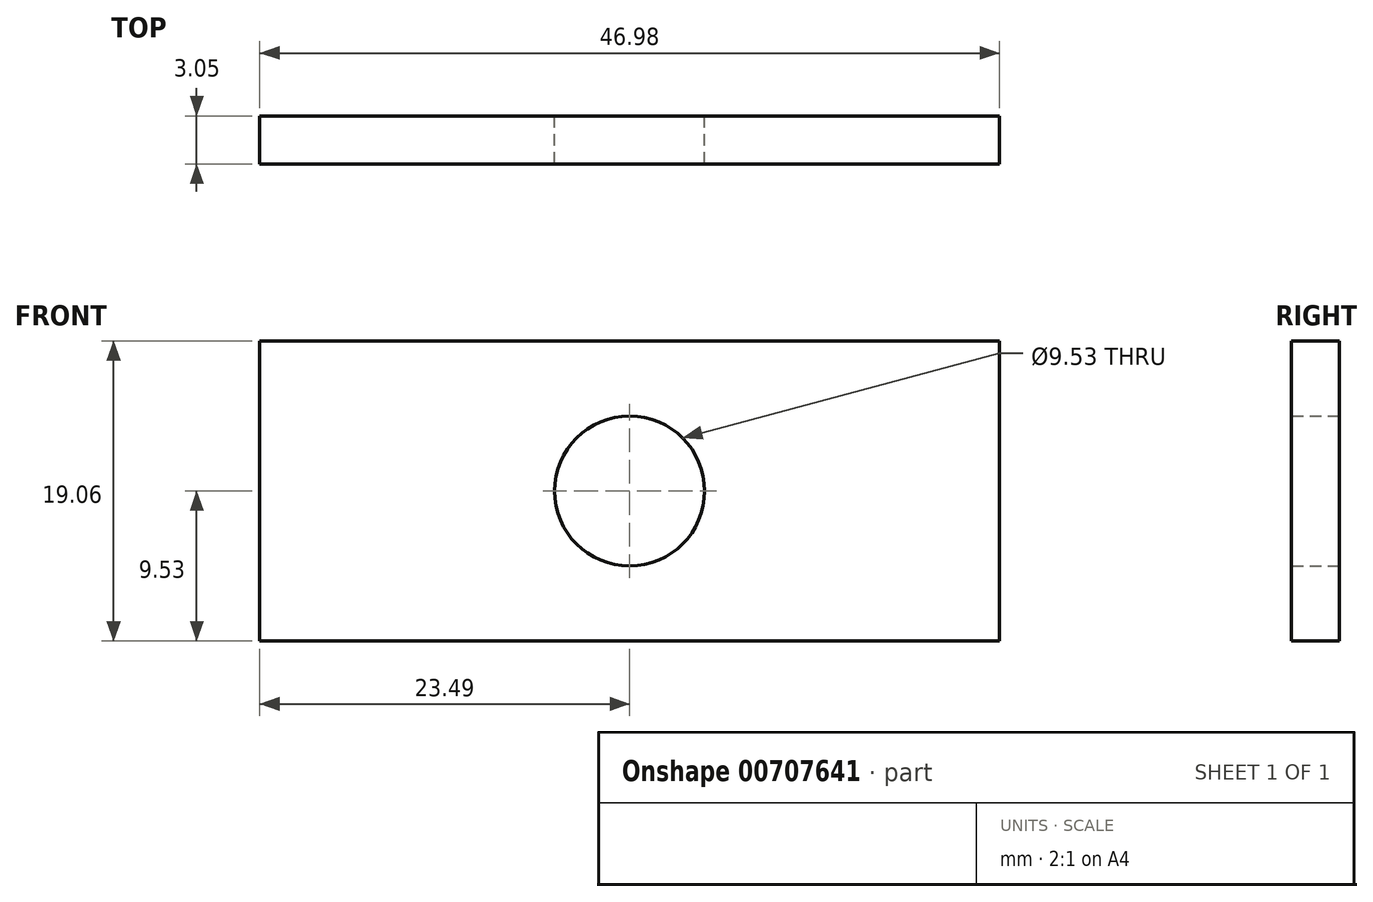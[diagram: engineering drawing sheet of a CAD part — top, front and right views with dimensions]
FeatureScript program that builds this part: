
annotation { "Feature Type Name" : "Feature", "Feature Type Description" : "" }
export const myFeature = defineFeature(function(context is Context, id is Id, definition is map)
    precondition{}
    {
        {
            var Q0;
            Q0=qCreatedBy(makeId("Front.planeOp"),FACE);
            var sketch = newSketch(context, id + "F0", { "sketchPlane" : qUnion([Q0])});
            skLineSegment(sketch, "E0.bottom", {"start": v(23.5, 9.52) * mm, "end": v(-23.5, 9.52) * mm});
            skLineSegment(sketch, "E0.top", {"start": v(23.5, -9.53) * mm, "end": v(-23.5, -9.53) * mm});
            skLineSegment(sketch, "E0.left", {"start": v(23.5, 9.52) * mm, "end": v(23.5, -9.53) * mm});
            skLineSegment(sketch, "E0.right", {"start": v(-23.5, 9.52) * mm, "end": v(-23.5, -9.53) * mm});
            skPoint(sketch, "E0.middle", {"position": v(0, 0) * mm});
            skCircle(sketch, "E1", {"center": v(0, 0) * mm, "radius": 4.76 * mm});
            skSolve(sketch);
        }
        {
            var Q0;
            Q0=qSketchRegion(id+"F0",true);
            extrude(context, id + "F1", {"entities" : qUnion([Q0]), "depth" : 3.05 * mm, "offsetDistance" : 25.4 * mm});
        }
    });
